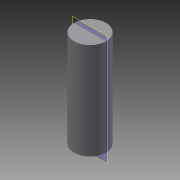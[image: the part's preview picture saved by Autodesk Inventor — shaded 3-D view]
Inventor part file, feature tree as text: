
AUTODESK INVENTOR PART (.ipt)
format: ipt  version: 2015 (Build 190159000, 159)  size: 87,552 bytes
history: native  units: mm
features: revolve x1, hole x1, sketch x1
ambient origin geometry x8: Origin, YZ Plane, XZ Plane, XY Plane, X Axis, Y Axis, Z Axis, Center Point
bodies: Solid1 (feature_tree)
feature tree (3):
  revolve  "Revolution1"  [1 undecoded]
  hole  "Hole1"  [1 undecoded]
  sketch  "Sketch1"  dims[d0=155.5mm d1=24.75mm d2=7.5mm d3=10.0mm d4=6.0mm d5=1.0mm d6=2.0mm d7=90.0deg d17=10.0mm d18=10.0mm d10=6.0mm d11=6.0mm d12=4.0mm d13=2.0mm d14=90.0deg d15=53.5mm d16=0.0mm]
note: 2 required parameter values undecoded (feature->parameter linkage not recoverable at this tier; creation-order binding heuristic only, values carry confidence <= 0.55)